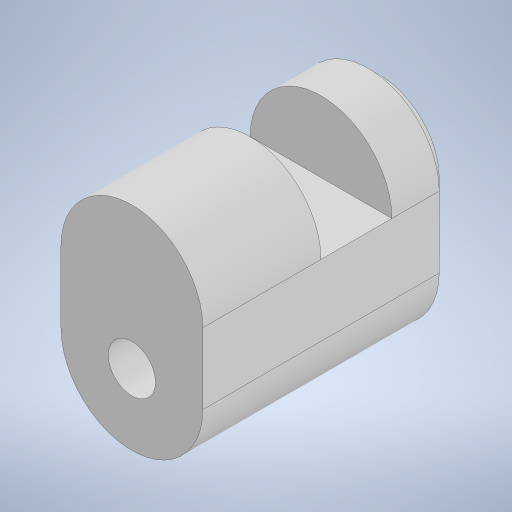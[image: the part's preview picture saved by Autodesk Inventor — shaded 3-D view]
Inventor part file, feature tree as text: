
AUTODESK INVENTOR PART (.ipt)
format: ipt  version: 2024.1 (Build 281209000, 209)  size: 236,032 bytes
history: native  units: mm
features: extrude x4, sketch x4, projected_geometry x3, chamfer x2
ambient origin geometry x8: Origin, YZ Plane, XZ Plane, XY Plane, X Axis, Y Axis, Z Axis, Center Point
bodies: Solid1 (feature_tree)
feature tree (13):
  extrude  "Extrusion1"  Depth=12.0mm
  extrude  "Extrusion2"  Depth=6.0mm
  extrude  "Extrusion3"  Depth=10.0mm TaperAngle=0.0deg
  extrude  "Extrusion4"  Depth=2.0mm TaperAngle=0.0deg
  chamfer  "Chamfer1"  Distance=2.0mm Angle=45.0deg
  chamfer  "Chamfer2"  Distance=2.0mm Angle=45.0deg
  sketch  "Sketch2"  dims[d0=12.0mm d1=4.0mm]
  sketch  "Sketch3"  dims[d2=21.0mm d3=0.0mm d4=6.0mm]
  projected_geometry  "Projected Loop1"
  sketch  "Sketch4"  dims[d5=6.0mm d6=10.0mm d7=0.0mm]
  projected_geometry  "Projected Loop2"
  sketch  "Sketch5"  dims[d8=5.0mm d9=0.0mm d10=6.4mm d11=0.0mm d12=3.0mm d13=2.0mm d14=45.0deg d15=1.0mm d16=2.0mm d17=45.0deg]
  projected_geometry  "Projected Loop3"
